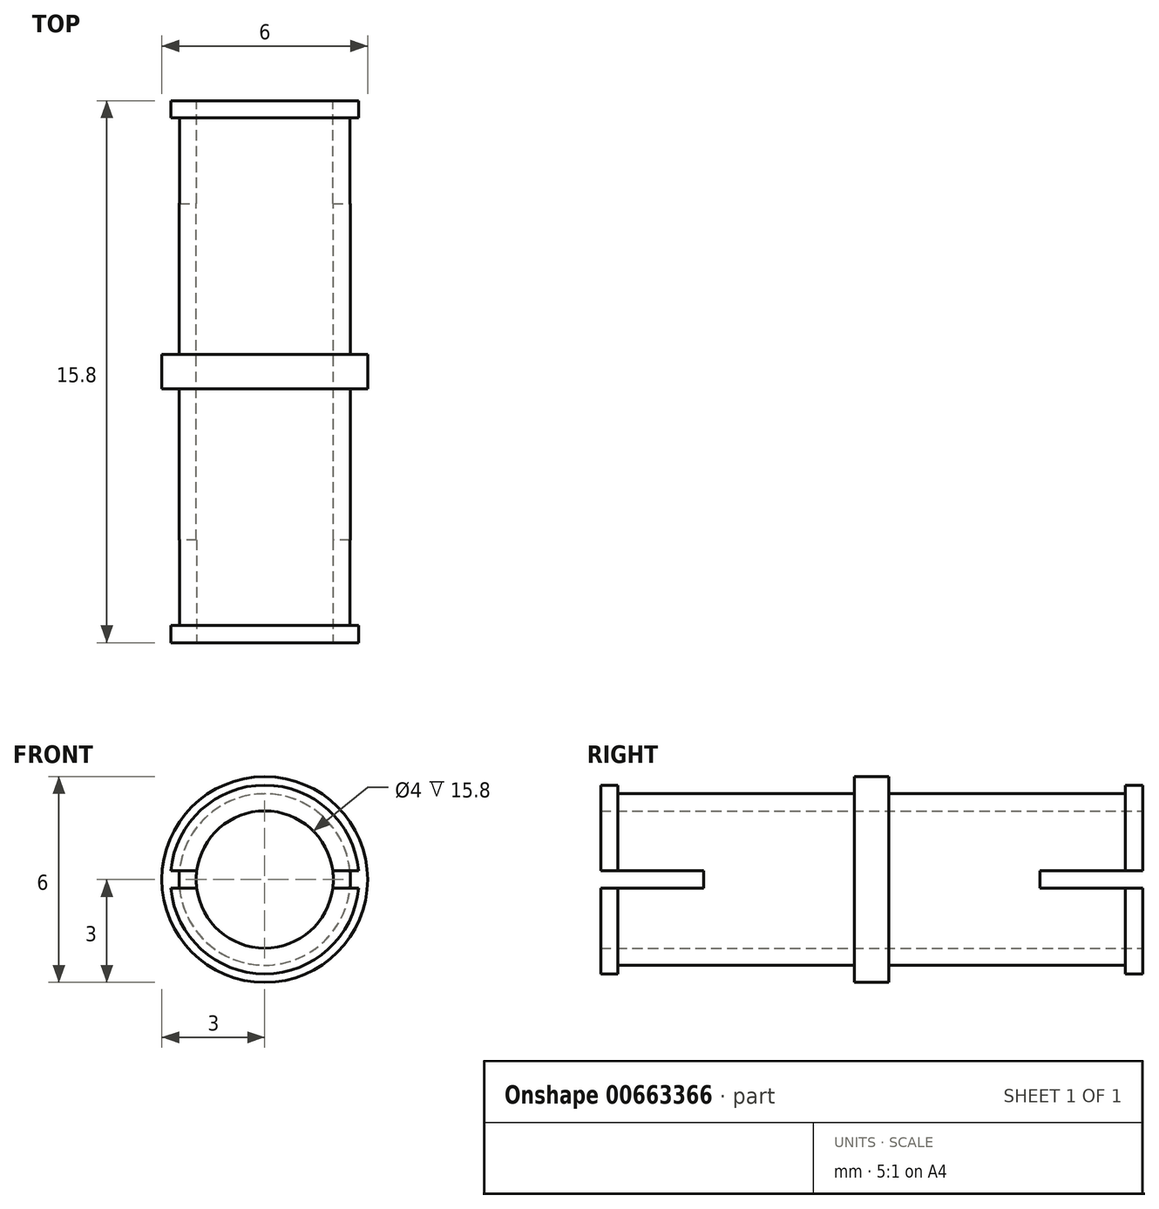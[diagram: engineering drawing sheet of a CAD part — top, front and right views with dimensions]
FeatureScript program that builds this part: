
annotation { "Feature Type Name" : "Feature", "Feature Type Description" : "" }
export const myFeature = defineFeature(function(context is Context, id is Id, definition is map)
    precondition{}
    {
        {
            var Q0;
            Q0=qCreatedBy(makeId("Front.planeOp"),FACE);
            var sketch = newSketch(context, id + "F0", { "sketchPlane" : qUnion([Q0])});
            skCircle(sketch, "E0", {"center": v(0, 0) * mm, "radius": 3 * mm});
            skCircle(sketch, "E1", {"center": v(0, 0) * mm, "radius": 2.5 * mm});
            skCircle(sketch, "E2", {"center": v(0, 0) * mm, "radius": 2 * mm});
            skSolve(sketch);
        }
        {
            var Q0;
            Q0=qSketchRegion(id+"F0",true);
            extrude(context, id + "F1", {"entities" : qUnion([Q0]), "endBound" : BoundingType.SYMMETRIC, "depth" : 1 * mm, "offsetDistance" : 25 * mm});
        }
        {
            var Q0;
            Q0=makeQuery(id+"F0.imprint","IMPRINT",FACE,{"disambiguationData":[TD([[makeQuery(id+"F0.imprint","IMPRINT",EDGE,{"derivedFrom":sQuery(id+"F0.wireOp",EDGE,"E1")}),1.0]])]});
            extrude(context, id + "F2", {"entities" : qUnion([Q0]), "operationType" : NewBodyOperationType.ADD, "endBound" : BoundingType.SYMMETRIC, "depth" : 15.9 * mm, "offsetDistance" : 25 * mm});
        }
        {
            var Q0;
            Q0=makeQuery(id+"F2.opExtrude","CAP_FACE",FACE,{"disambiguationData":[OSD([sQuery(id+"F0.wireOp",EDGE,"E1"),sQuery(id+"F0.wireOp",EDGE,"E2")])],"isStart":false});
            var sketch = newSketch(context, id + "F3", { "sketchPlane" : qUnion([Q0])});
            skCircle(sketch, "E3", {"center": v(0, 0) * mm, "radius": 2.75 * mm});
            skSolve(sketch);
        }
        {
            var Q0;
            Q0=makeQuery(id+"F3.imprint","IMPRINT",FACE,{"disambiguationData":[TD([[makeQuery(id+"F3.imprint","IMPRINT",EDGE,{"derivedFrom":sQuery(id+"F3.wireOp",EDGE,"E3")}),1.0]])]});
            var Q1;
            Q1=makeQuery(id+"F3.imprint","IMPRINT",FACE,{"disambiguationData":[TD([[makeQuery(id+"F3.imprint","IMPRINT",EDGE,{"derivedFrom":makeQuery(id+"F2.opExtrude","CAP_EDGE",EDGE,{"disambiguationData":[OSD([sQuery(id+"F0.wireOp",EDGE,"E1")])],"isStart":false})}),1.0]])]});
            extrude(context, id + "F4", {"entities" : qUnion([Q0, Q1]), "operationType" : NewBodyOperationType.ADD, "oppositeDirection" : true, "depth" : 1 * mm, "offsetDistance" : 25 * mm});
        }
        {
            var Q0;
            {var subQ0=sQuery(id+"F0.wireOp",EDGE,"E2");Q0=makeQuery(id+"F4.boolean.opBoolean","MERGE",FACE,{"derivedFrom":[makeQuery(id+"F2.opExtrude","CAP_FACE",FACE,{"disambiguationData":[OSD([sQuery(id+"F0.wireOp",EDGE,"E1"),subQ0])],"isStart":false}),makeQuery(id+"F4.opExtrude","CAP_FACE",FACE,{"disambiguationData":[OSD([subQ0,sQuery(id+"F3.wireOp",EDGE,"E3")])],"isStart":true})]});}
            var sketch = newSketch(context, id + "F5", { "sketchPlane" : qUnion([Q0])});
            skLineSegment(sketch, "E4.bottom", {"start": v(2.74, -0.25) * mm, "end": v(1.98, -0.25) * mm});
            skLineSegment(sketch, "E4.top", {"start": v(2.74, 0.25) * mm, "end": v(1.98, 0.25) * mm});
            skPoint(sketch, "E4.middle", {"position": v(0, 0) * mm});
            skArc(sketch, "E5.0", {"start": v(-1.98, 0.25) * mm, "mid": v(-2, 0) * mm, "end": v(-1.98, -0.25) * mm});
            skArc(sketch, "E6.0", {"start": v(-2.74, 0.25) * mm, "mid": v(-2.75, 0) * mm, "end": v(-2.74, -0.25) * mm});
            skLineSegment(sketch, "E7.trimOffspring", {"start": v(-1.98, 0.25) * mm, "end": v(-2.74, 0.25) * mm});
            skLineSegment(sketch, "E8.trimOffspring", {"start": v(-1.98, -0.25) * mm, "end": v(-2.74, -0.25) * mm});
            skPoint(sketch, "E9.orphan", {"position": v(3, -0.25) * mm});
            skPoint(sketch, "E10.orphan", {"position": v(3, 0.25) * mm});
            skPoint(sketch, "E4.right.end.orphan", {"position": v(-3, 0.25) * mm});
            skPoint(sketch, "E11.orphan", {"position": v(-3, -0.25) * mm});
            skArc(sketch, "E12.trimOffspring", {"start": v(1.98, -0.25) * mm, "mid": v(2, 0) * mm, "end": v(1.98, 0.25) * mm});
            skArc(sketch, "E13.trimOffspring", {"start": v(2.74, -0.25) * mm, "mid": v(2.75, 0) * mm, "end": v(2.74, 0.25) * mm});
            skSolve(sketch);
        }
        {
            var Q0;
            Q0=qSketchRegion(id+"F5",true);
            extrude(context, id + "F6", {"entities" : qUnion([Q0]), "operationType" : NewBodyOperationType.REMOVE, "oppositeDirection" : true, "depth" : 3 * mm, "offsetDistance" : 25 * mm});
        }
        {
            var Q0;
            Q0=makeQuery(id+"F2.opExtrude","CAP_FACE",FACE,{"disambiguationData":[OSD([sQuery(id+"F0.wireOp",EDGE,"E1"),sQuery(id+"F0.wireOp",EDGE,"E2")])],"isStart":true});
            var sketch = newSketch(context, id + "F7", { "sketchPlane" : qUnion([Q0])});
            skCircle(sketch, "E14", {"center": v(0, 0) * mm, "radius": 2.75 * mm});
            skSolve(sketch);
        }
        {
            var Q0;
            Q0=makeQuery(id+"F7.imprint","IMPRINT",FACE,{"disambiguationData":[TD([[makeQuery(id+"F7.imprint","IMPRINT",EDGE,{"derivedFrom":sQuery(id+"F7.wireOp",EDGE,"E14")}),1.0]])]});
            var Q1;
            Q1=makeQuery(id+"F7.imprint","IMPRINT",FACE,{"disambiguationData":[TD([[makeQuery(id+"F7.imprint","IMPRINT",EDGE,{"derivedFrom":makeQuery(id+"F2.opExtrude","CAP_EDGE",EDGE,{"disambiguationData":[OSD([sQuery(id+"F0.wireOp",EDGE,"E1")])],"isStart":true})}),-1.0]])]});
            extrude(context, id + "F8", {"entities" : qUnion([Q0, Q1]), "operationType" : NewBodyOperationType.ADD, "oppositeDirection" : true, "depth" : 1 * mm, "offsetDistance" : 25 * mm});
        }
        {
            var Q0;
            {var subQ0=sQuery(id+"F0.wireOp",EDGE,"E2");Q0=makeQuery(id+"F8.boolean.opBoolean","MERGE",FACE,{"derivedFrom":[makeQuery(id+"F2.opExtrude","CAP_FACE",FACE,{"disambiguationData":[OSD([sQuery(id+"F0.wireOp",EDGE,"E1"),subQ0])],"isStart":true}),makeQuery(id+"F8.opExtrude","CAP_FACE",FACE,{"disambiguationData":[OSD([subQ0,sQuery(id+"F7.wireOp",EDGE,"E14")])],"isStart":true})]});}
            var sketch = newSketch(context, id + "F9", { "sketchPlane" : qUnion([Q0])});
            skLineSegment(sketch, "E15.bottom", {"start": v(2.74, 0.25) * mm, "end": v(1.98, 0.25) * mm});
            skLineSegment(sketch, "E15.top", {"start": v(2.74, -0.25) * mm, "end": v(1.98, -0.25) * mm});
            skPoint(sketch, "E15.middle", {"position": v(0, 0) * mm});
            skArc(sketch, "E16.0", {"start": v(-1.98, 0.25) * mm, "mid": v(-2, 0) * mm, "end": v(-1.98, -0.25) * mm});
            skArc(sketch, "E17.0", {"start": v(2.74, -0.25) * mm, "mid": v(0, 2.75) * mm, "end": v(-2.74, -0.25) * mm});
            skLineSegment(sketch, "E18.trimOffspring", {"start": v(-1.98, 0.25) * mm, "end": v(-2.74, 0.25) * mm});
            skLineSegment(sketch, "E19.trimOffspring", {"start": v(-1.98, -0.25) * mm, "end": v(-2.74, -0.25) * mm});
            skPoint(sketch, "E15.left.end.orphan", {"position": v(3, -0.25) * mm});
            skPoint(sketch, "E15.left.start.orphan", {"position": v(3, 0.25) * mm});
            skPoint(sketch, "E15.right.start.orphan", {"position": v(-3, 0.25) * mm});
            skPoint(sketch, "E20.orphan", {"position": v(-3, -0.25) * mm});
            skArc(sketch, "E21.trimOffspring", {"start": v(1.98, -0.25) * mm, "mid": v(2, 0) * mm, "end": v(1.98, 0.25) * mm});
            skSolve(sketch);
        }
        {
            var Q0;
            Q0=qSketchRegion(id+"F9",true);
            extrude(context, id + "F10", {"entities" : qUnion([Q0]), "operationType" : NewBodyOperationType.REMOVE, "oppositeDirection" : true, "depth" : 3 * mm, "offsetDistance" : 25 * mm});
        }
        {
            var Q0;
            {var subQ0=sQuery(id+"F0.wireOp",EDGE,"E2");var subQ1=sQuery(id+"F7.wireOp",EDGE,"E14");Q0=makeQuery(id+"F10.boolean.opBoolean","SPLIT",FACE,{"disambiguationData":[TD([makeQuery(id+"F10.opExtrude","SWEPT_FACE",FACE,{"disambiguationData":[OSD([sQuery(id+"F9.wireOp",EDGE,"E15.bottom")])]})])],"derivedFrom":makeQuery(id+"F8.boolean.opBoolean","MERGE",FACE,{"derivedFrom":[makeQuery(id+"F2.opExtrude","CAP_FACE",FACE,{"disambiguationData":[OSD([sQuery(id+"F0.wireOp",EDGE,"E1"),subQ0])],"isStart":true}),makeQuery(id+"F8.opExtrude","CAP_FACE",FACE,{"disambiguationData":[OSD([subQ0,subQ1])],"isStart":true})]})});}
            var Q1;
            Q1=makeQuery(id+"F10.boolean.opBoolean","COPY",FACE,{"derivedFrom":makeQuery(id+"F10.opExtrude","CAP_FACE",FACE,{"disambiguationData":[OSD([sQuery(id+"F9.wireOp",EDGE,"E16.0"),sQuery(id+"F9.wireOp",EDGE,"E17.0"),sQuery(id+"F9.wireOp",EDGE,"E18.trimOffspring"),sQuery(id+"F9.wireOp",EDGE,"E19.trimOffspring")])],"isStart":false})});
            var Q2;
            {var subQ0=sQuery(id+"F0.wireOp",EDGE,"E2");var subQ1=sQuery(id+"F7.wireOp",EDGE,"E14");Q2=makeQuery(id+"F10.boolean.opBoolean","SPLIT",FACE,{"disambiguationData":[TD([makeQuery(id+"F10.opExtrude","SWEPT_FACE",FACE,{"disambiguationData":[OSD([sQuery(id+"F9.wireOp",EDGE,"E15.top")])]})])],"derivedFrom":makeQuery(id+"F8.boolean.opBoolean","MERGE",FACE,{"derivedFrom":[makeQuery(id+"F2.opExtrude","CAP_FACE",FACE,{"disambiguationData":[OSD([sQuery(id+"F0.wireOp",EDGE,"E1"),subQ0])],"isStart":true}),makeQuery(id+"F8.opExtrude","CAP_FACE",FACE,{"disambiguationData":[OSD([subQ0,subQ1])],"isStart":true})]})});}
            var Q3;
            Q3=makeQuery(id+"F10.boolean.opBoolean","COPY",FACE,{"derivedFrom":makeQuery(id+"F10.opExtrude","CAP_FACE",FACE,{"disambiguationData":[OSD([sQuery(id+"F9.wireOp",EDGE,"E15.bottom"),sQuery(id+"F9.wireOp",EDGE,"E15.top"),sQuery(id+"F9.wireOp",EDGE,"E17.0"),sQuery(id+"F9.wireOp",EDGE,"E21.trimOffspring")])],"isStart":false})});
            extrude(context, id + "F11", {"entities" : qUnion([Q0, Q1, Q2, Q3]), "operationType" : NewBodyOperationType.REMOVE, "oppositeDirection" : true, "depth" : 0.05 * mm, "offsetDistance" : 25 * mm});
        }
        {
            var Q0;
            {var subQ0=sQuery(id+"F0.wireOp",EDGE,"E2");var subQ1=sQuery(id+"F3.wireOp",EDGE,"E3");Q0=makeQuery(id+"F6.boolean.opBoolean","SPLIT",FACE,{"disambiguationData":[TD([makeQuery(id+"F6.opExtrude","SWEPT_FACE",FACE,{"disambiguationData":[OSD([sQuery(id+"F5.wireOp",EDGE,"E4.top")])]})])],"derivedFrom":makeQuery(id+"F4.boolean.opBoolean","MERGE",FACE,{"derivedFrom":[makeQuery(id+"F2.opExtrude","CAP_FACE",FACE,{"disambiguationData":[OSD([sQuery(id+"F0.wireOp",EDGE,"E1"),subQ0])],"isStart":false}),makeQuery(id+"F4.opExtrude","CAP_FACE",FACE,{"disambiguationData":[OSD([subQ0,subQ1])],"isStart":true})]})});}
            var Q1;
            Q1=makeQuery(id+"F6.boolean.opBoolean","COPY",FACE,{"derivedFrom":makeQuery(id+"F6.opExtrude","CAP_FACE",FACE,{"disambiguationData":[OSD([sQuery(id+"F5.wireOp",EDGE,"E5.0"),sQuery(id+"F5.wireOp",EDGE,"E6.0"),sQuery(id+"F5.wireOp",EDGE,"E7.trimOffspring"),sQuery(id+"F5.wireOp",EDGE,"E8.trimOffspring")])],"isStart":false})});
            var Q2;
            {var subQ0=sQuery(id+"F0.wireOp",EDGE,"E2");var subQ1=sQuery(id+"F3.wireOp",EDGE,"E3");Q2=makeQuery(id+"F6.boolean.opBoolean","SPLIT",FACE,{"disambiguationData":[TD([makeQuery(id+"F6.opExtrude","SWEPT_FACE",FACE,{"disambiguationData":[OSD([sQuery(id+"F5.wireOp",EDGE,"E4.bottom")])]})])],"derivedFrom":makeQuery(id+"F4.boolean.opBoolean","MERGE",FACE,{"derivedFrom":[makeQuery(id+"F2.opExtrude","CAP_FACE",FACE,{"disambiguationData":[OSD([sQuery(id+"F0.wireOp",EDGE,"E1"),subQ0])],"isStart":false}),makeQuery(id+"F4.opExtrude","CAP_FACE",FACE,{"disambiguationData":[OSD([subQ0,subQ1])],"isStart":true})]})});}
            var Q3;
            Q3=makeQuery(id+"F6.boolean.opBoolean","COPY",FACE,{"derivedFrom":makeQuery(id+"F6.opExtrude","CAP_FACE",FACE,{"disambiguationData":[OSD([sQuery(id+"F5.wireOp",EDGE,"E4.bottom"),sQuery(id+"F5.wireOp",EDGE,"E4.top"),sQuery(id+"F5.wireOp",EDGE,"E12.trimOffspring"),sQuery(id+"F5.wireOp",EDGE,"E13.trimOffspring")])],"isStart":false})});
            extrude(context, id + "F12", {"entities" : qUnion([Q0, Q1, Q2, Q3]), "operationType" : NewBodyOperationType.REMOVE, "oppositeDirection" : true, "depth" : 0.05 * mm, "offsetDistance" : 25 * mm});
        }
        {
            var Q0;
            {var subQ0=sQuery(id+"F7.wireOp",EDGE,"E14");Q0=makeQuery(id+"F10.boolean.opBoolean","SPLIT",FACE,{"disambiguationData":[TD([makeQuery(id+"F10.opExtrude","SWEPT_FACE",FACE,{"disambiguationData":[OSD([sQuery(id+"F9.wireOp",EDGE,"E15.bottom")])]})])],"derivedFrom":makeQuery(id+"F8.opExtrude","CAP_FACE",FACE,{"disambiguationData":[OSD([sQuery(id+"F0.wireOp",EDGE,"E2"),subQ0])],"isStart":false})});}
            var Q1;
            {var subQ0=sQuery(id+"F7.wireOp",EDGE,"E14");Q1=makeQuery(id+"F10.boolean.opBoolean","SPLIT",FACE,{"disambiguationData":[TD([makeQuery(id+"F10.opExtrude","SWEPT_FACE",FACE,{"disambiguationData":[OSD([sQuery(id+"F9.wireOp",EDGE,"E15.top")])]})])],"derivedFrom":makeQuery(id+"F8.opExtrude","CAP_FACE",FACE,{"disambiguationData":[OSD([sQuery(id+"F0.wireOp",EDGE,"E2"),subQ0])],"isStart":false})});}
            extrude(context, id + "F13", {"entities" : qUnion([Q0, Q1]), "operationType" : NewBodyOperationType.REMOVE, "oppositeDirection" : true, "depth" : 0.45 * mm, "offsetDistance" : 25 * mm});
        }
        {
            var Q0;
            {var subQ0=sQuery(id+"F3.wireOp",EDGE,"E3");Q0=makeQuery(id+"F6.boolean.opBoolean","SPLIT",FACE,{"disambiguationData":[TD([makeQuery(id+"F6.opExtrude","SWEPT_FACE",FACE,{"disambiguationData":[OSD([sQuery(id+"F5.wireOp",EDGE,"E4.top")])]})])],"derivedFrom":makeQuery(id+"F4.opExtrude","CAP_FACE",FACE,{"disambiguationData":[OSD([sQuery(id+"F0.wireOp",EDGE,"E2"),subQ0])],"isStart":false})});}
            var Q1;
            {var subQ0=sQuery(id+"F3.wireOp",EDGE,"E3");Q1=makeQuery(id+"F6.boolean.opBoolean","SPLIT",FACE,{"disambiguationData":[TD([makeQuery(id+"F6.opExtrude","SWEPT_FACE",FACE,{"disambiguationData":[OSD([sQuery(id+"F5.wireOp",EDGE,"E4.bottom")])]})])],"derivedFrom":makeQuery(id+"F4.opExtrude","CAP_FACE",FACE,{"disambiguationData":[OSD([sQuery(id+"F0.wireOp",EDGE,"E2"),subQ0])],"isStart":false})});}
            extrude(context, id + "F14", {"entities" : qUnion([Q0, Q1]), "operationType" : NewBodyOperationType.REMOVE, "oppositeDirection" : true, "depth" : 0.45 * mm, "offsetDistance" : 25 * mm});
        }
    });
